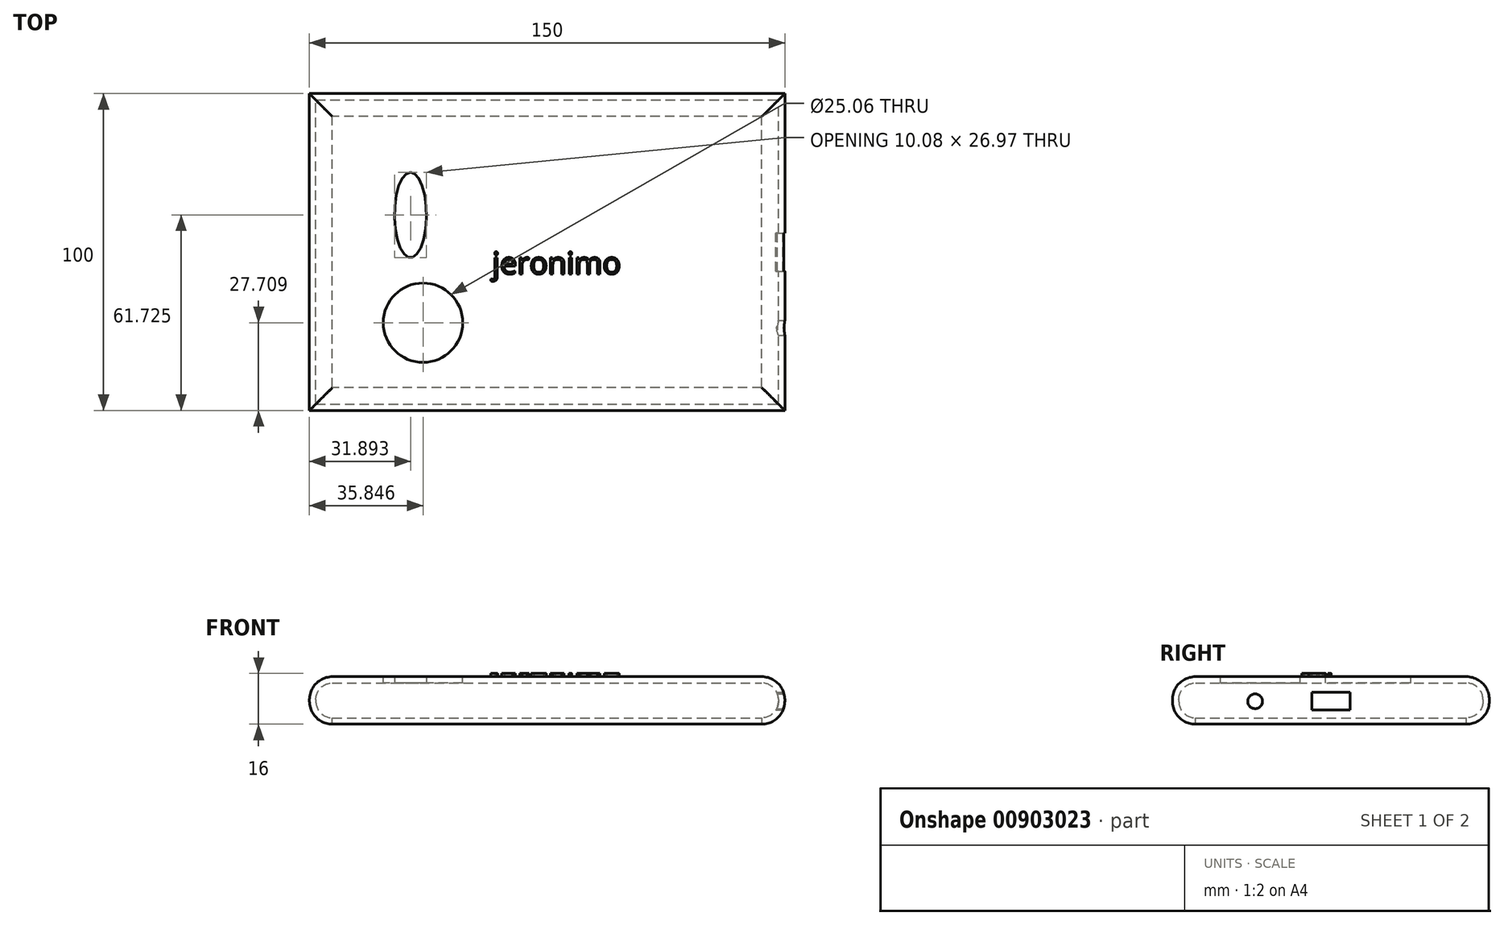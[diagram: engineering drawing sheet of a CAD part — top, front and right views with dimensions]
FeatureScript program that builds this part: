
annotation { "Feature Type Name" : "Feature", "Feature Type Description" : "" }
export const myFeature = defineFeature(function(context is Context, id is Id, definition is map)
    precondition{}
    {
        {
            var Q0;
            Q0=qCreatedBy(makeId("Top.planeOp"),FACE);
            var sketch = newSketch(context, id + "F0", { "sketchPlane" : qUnion([Q0])});
            skLineSegment(sketch, "E0.bottom", {"start": v(75, -50) * mm, "end": v(-75, -50) * mm});
            skLineSegment(sketch, "E0.top", {"start": v(75, 50) * mm, "end": v(-75, 50) * mm});
            skLineSegment(sketch, "E0.left", {"start": v(75, -50) * mm, "end": v(75, 50) * mm});
            skLineSegment(sketch, "E0.right", {"start": v(-75, -50) * mm, "end": v(-75, 50) * mm});
            skPoint(sketch, "E0.middle", {"position": v(0, 0) * mm});
            skSolve(sketch);
        }
        {
            var Q0;
            Q0 = qSketchRegion(id + "F0", true);
            extrude(context, id + "F1", {"entities" : qUnion([Q0]), "depth" : 15 * mm, "offsetDistance" : 25 * mm});
        }
        {
            var Q0;
            Q0=makeQuery(id+"F1.opExtrude","CAP_FACE",FACE,{"disambiguationData":[OSD([sQuery(id+"F0.wireOp",EDGE,"E0.bottom"),sQuery(id+"F0.wireOp",EDGE,"E0.top"),sQuery(id+"F0.wireOp",EDGE,"E0.left"),sQuery(id+"F0.wireOp",EDGE,"E0.right")])],"isStart":false});
            var Q1;
            Q1=makeQuery(id+"F1.opExtrude","CAP_EDGE",EDGE,{"disambiguationData":[OSD([sQuery(id+"F0.wireOp",EDGE,"E0.bottom")])],"isStart":true});
            var Q2;
            Q2=makeQuery(id+"F1.opExtrude","CAP_EDGE",EDGE,{"disambiguationData":[OSD([sQuery(id+"F0.wireOp",EDGE,"E0.top")])],"isStart":true});
            var Q3;
            Q3=makeQuery(id+"F1.opExtrude","CAP_EDGE",EDGE,{"disambiguationData":[OSD([sQuery(id+"F0.wireOp",EDGE,"E0.right")])],"isStart":true});
            var Q4;
            Q4=makeQuery(id+"F1.opExtrude","CAP_EDGE",EDGE,{"disambiguationData":[OSD([sQuery(id+"F0.wireOp",EDGE,"E0.left")])],"isStart":true});
            fillet(context, id + "F2", {"entities" : qUnion([Q0, Q1, Q2, Q3, Q4]), "radius" : 7.24 * mm, "tangentPropagation" : true, "allowEdgeOverflow" : false});
        }
        {
            var Q0;
            Q0=makeQuery(id+"F1.opExtrude","CAP_FACE",FACE,{"disambiguationData":[OSD([sQuery(id+"F0.wireOp",EDGE,"E0.bottom"),sQuery(id+"F0.wireOp",EDGE,"E0.top"),sQuery(id+"F0.wireOp",EDGE,"E0.left"),sQuery(id+"F0.wireOp",EDGE,"E0.right")])],"isStart":true});
            shell(context, id + "F3", {"entities" : qUnion([Q0]), "thickness" : 2 * mm});
        }
        {
            var Q0;
            Q0=makeQuery(id+"F1.opExtrude","CAP_FACE",FACE,{"disambiguationData":[OSD([sQuery(id+"F0.wireOp",EDGE,"E0.bottom"),sQuery(id+"F0.wireOp",EDGE,"E0.top"),sQuery(id+"F0.wireOp",EDGE,"E0.left"),sQuery(id+"F0.wireOp",EDGE,"E0.right")])],"isStart":false});
            var sketch = newSketch(context, id + "F4", { "sketchPlane" : qUnion([Q0])});
            skCircle(sketch, "E1", {"center": v(-39.15, -22.3) * mm, "radius": 12.53 * mm});
            skPoint(sketch, "E1.first.point", {"position": v(-51.64, -23.33) * mm});
            skPoint(sketch, "E1.second.point", {"position": v(-26.7, -23.74) * mm});
            skPoint(sketch, "E1.third.point", {"position": v(-37.31, -34.69) * mm});
            skEllipse(sketch, "E2", {"center": v(-43.1, 11.73) * mm, "majorRadius": 13.49 * mm, "minorRadius": 5.04 * mm, "majorAxis": v(0, 1)});
            skSolve(sketch);
        }
        {
            var Q0;
            Q0 = qSketchRegion(id + "F4", true);
            extrude(context, id + "F5", {"entities" : qUnion([Q0]), "operationType" : NewBodyOperationType.REMOVE, "oppositeDirection" : true, "depth" : 25 * mm, "offsetDistance" : 25 * mm});
        }
        {
            var Q0;
            Q0=makeQuery(id+"F1.opExtrude","SWEPT_FACE",FACE,{"disambiguationData":[OSD([sQuery(id+"F0.wireOp",EDGE,"E0.left")])]});
            var sketch = newSketch(context, id + "F6", { "sketchPlane" : qUnion([Q0])});
            skLineSegment(sketch, "E3.bottom", {"start": v(6.05, 4.45) * mm, "end": v(-6.05, 4.45) * mm});
            skLineSegment(sketch, "E3.top", {"start": v(6.05, 10.04) * mm, "end": v(-6.05, 10.04) * mm});
            skLineSegment(sketch, "E3.left", {"start": v(6.05, 4.45) * mm, "end": v(6.05, 10.04) * mm});
            skLineSegment(sketch, "E3.right", {"start": v(-6.05, 4.45) * mm, "end": v(-6.05, 10.04) * mm});
            skPoint(sketch, "E3.middle", {"position": v(0, 7.24) * mm});
            skCircle(sketch, "E4", {"center": v(-23.92, 7.24) * mm, "radius": 2.33 * mm});
            skSolve(sketch);
        }
        {
            var Q0;
            Q0 = qSketchRegion(id + "F6", true);
            extrude(context, id + "F7", {"entities" : qUnion([Q0]), "operationType" : NewBodyOperationType.REMOVE, "oppositeDirection" : true, "depth" : 25 * mm, "offsetDistance" : 25 * mm});
        }
        {
            var Q0;
            Q0=makeQuery(id+"F1.opExtrude","CAP_FACE",FACE,{"disambiguationData":[OSD([sQuery(id+"F0.wireOp",EDGE,"E0.bottom"),sQuery(id+"F0.wireOp",EDGE,"E0.top"),sQuery(id+"F0.wireOp",EDGE,"E0.left"),sQuery(id+"F0.wireOp",EDGE,"E0.right")])],"isStart":false});
            var sketch = newSketch(context, id + "F8", { "sketchPlane" : qUnion([Q0])});
            skText(sketch, "E5", { "text": "jeronimo", "fontName": "OpenSans-Regular.ttf"});
            const initialGuessF8  = {"E5": [-0.01729, -0.00691, 1, 0, 0.00691]};
            skSetInitialGuess(sketch, initialGuessF8);
            skSolve(sketch);
        }
        {
            var Q0;
            Q0 = qSketchRegion(id + "F8", true);
            extrude(context, id + "F9", {"entities" : qUnion([Q0]), "operationType" : NewBodyOperationType.ADD, "depth" : 1 * mm, "offsetDistance" : 25 * mm});
        }
    });
